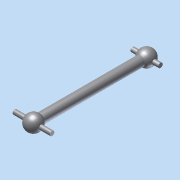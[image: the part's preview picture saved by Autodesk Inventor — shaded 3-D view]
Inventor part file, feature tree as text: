
AUTODESK INVENTOR PART (.ipt)
format: ipt  version: 2011 SP1 (Build 150282100, 282)  size: 109,056 bytes
history: native  units: in
note: dims shown in document units (in); Inventor stores cm internally (conversion verified against a paired STEP export)
features: sketch x4, extrude x3, plane x2, mirror x2, projected_geometry x2, revolve x1
ambient origin geometry x8: Origin, YZ Plane, XZ Plane, XY Plane, X Axis, Y Axis, Z Axis, Center Point
bodies: Solid1 (feature_tree)
feature tree (14):
  extrude  "Extrusion1"  Depth=1.69in TaperAngle=0.0deg
  revolve  "Revolution1"  Angle=90.0deg
  plane  "Work Plane1"
  extrude  "Extrusion2"  Depth=0.075in
  mirror  "Mirror1"
  plane  "Work Plane2"
  extrude  "Extrusion3"  Depth=0.235in
  mirror  "Mirror2"
  sketch  "Sketch1"  dims[d0=0.16in d1=1.69in d2=0.0in]
  sketch  "Sketch2"  dims[d3=0.27in d4=90.0deg]
  sketch  "Sketch3"  dims[d5=0.315in d6=0.075in]
  sketch  "Sketch4"  dims[d7=1.69in d8=0.0in d9=0.235in d10=0.075in d11=1.69in d12=0.0in]
  projected_geometry  "Project Cut Edges1"
  projected_geometry  "Project Cut Edges2"
